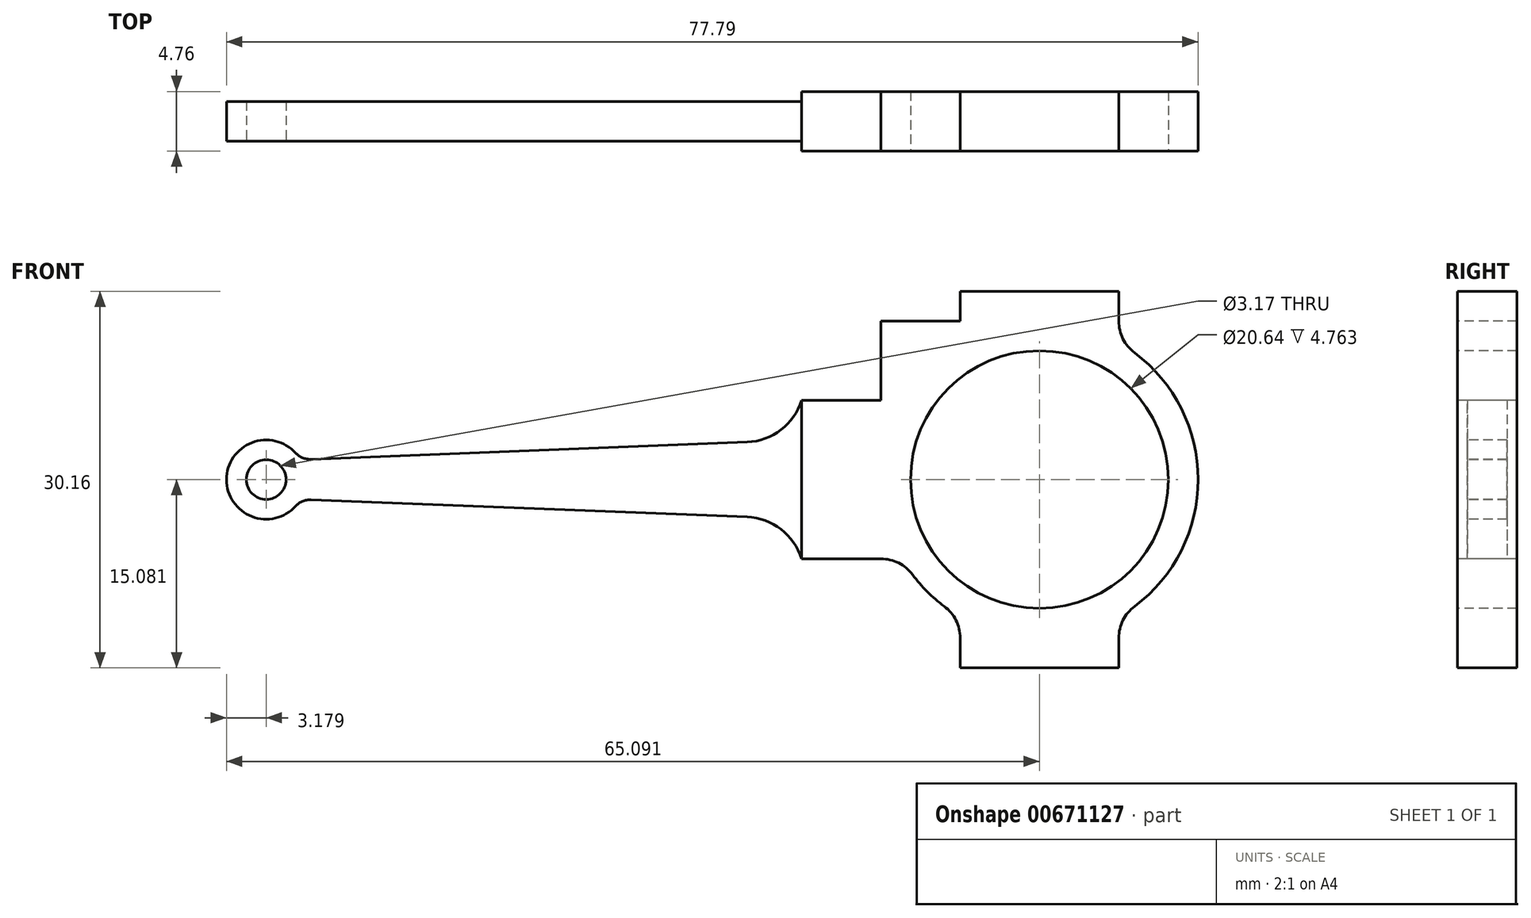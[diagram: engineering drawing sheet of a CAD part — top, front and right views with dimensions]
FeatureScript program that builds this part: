
annotation { "Feature Type Name" : "Feature", "Feature Type Description" : "" }
export const myFeature = defineFeature(function(context is Context, id is Id, definition is map)
    precondition{}
    {
        {
            var Q0;
            Q0=qCreatedBy(makeId("Top.planeOp"),FACE);
            var sketch = newSketch(context, id + "F0", { "sketchPlane" : qUnion([Q0])});
            skLineSegment(sketch, "E0", {"start": v(-28.4, 19.75) * mm, "end": v(17.64, 19.75) * mm});
            skLineSegment(sketch, "E1", {"start": v(17.64, 19.75) * mm, "end": v(17.64, 20.54) * mm});
            skLineSegment(sketch, "E2", {"start": v(17.64, 20.54) * mm, "end": v(49.4, 20.54) * mm});
            skLineSegment(sketch, "E3", {"start": v(49.4, 20.54) * mm, "end": v(49.4, 15.78) * mm});
            skLineSegment(sketch, "E4", {"start": v(49.4, 15.78) * mm, "end": v(17.64, 15.78) * mm});
            skLineSegment(sketch, "E5", {"start": v(17.64, 15.78) * mm, "end": v(17.64, 16.57) * mm});
            skLineSegment(sketch, "E6", {"start": v(17.64, 16.57) * mm, "end": v(-28.4, 16.57) * mm});
            skLineSegment(sketch, "E7", {"start": v(-28.4, 16.57) * mm, "end": v(-28.4, 19.75) * mm});
            skSolve(sketch);
        }
        {
            var Q0;
            Q0=qSketchRegion(id+"F0",true);
            extrude(context, id + "F1", {"entities" : qUnion([Q0]), "depth" : 30.16 * mm});
        }
        {
            var Q0;
            Q0=makeQuery(id+"F1.opExtrude","SWEPT_FACE",FACE,{"disambiguationData":[OSD([sQuery(id+"F0.wireOp",EDGE,"E6")])]});
            var sketch = newSketch(context, id + "F2", { "sketchPlane" : qUnion([Q0])});
            skCircle(sketch, "E8", {"center": v(-25.22, 15.08) * mm, "radius": 1.59 * mm});
            skCircle(sketch, "E9", {"center": v(-25.22, 15.08) * mm, "radius": 3.18 * mm});
            skLineSegment(sketch, "E10", {"start": v(-25.22, 15.08) * mm, "end": v(17.64, 15.08) * mm, "construction": true});
            skLineSegment(sketch, "E11", {"start": v(-22.47, 16.67) * mm, "end": v(17.64, 18.26) * mm});
            skLineSegment(sketch, "E12", {"start": v(-22.47, 13.5) * mm, "end": v(17.64, 11.9) * mm});
            skArc(sketch, "E13", {"start": v(-22.87, 17.22) * mm, "mid": v(-22.31, 16.82) * mm, "end": v(-21.64, 16.7) * mm});
            skArc(sketch, "E14", {"start": v(-21.64, 13.46) * mm, "mid": v(-22.31, 13.34) * mm, "end": v(-22.87, 12.94) * mm});
            skArc(sketch, "E15", {"start": v(13.28, 18.08) * mm, "mid": v(16, 19.06) * mm, "end": v(17.64, 21.43) * mm});
            skArc(sketch, "E16", {"start": v(17.64, 8.73) * mm, "mid": v(16, 11.1) * mm, "end": v(13.28, 12.08) * mm});
            skSolve(sketch);
        }
        {
            var Q0;
            Q0=makeQuery(id+"F2.imprint","IMPRINT",FACE,{"disambiguationData":[TD([[makeQuery(id+"F2.imprint","IMPRINT",EDGE,{"derivedFrom":sQuery(id+"F2.wireOp",EDGE,"E8")}),1.0]])]});
            var Q1;
            {var subQ1=sQuery(id+"F2.wireOp",EDGE,"E13");Q1=makeQuery(id+"F2.imprint","IMPRINT",FACE,{"disambiguationData":[TD([[makeQuery(id+"F2.imprint","IMPRINT",EDGE,{"derivedFrom":subQ1}),1.0]])]});}
            var Q2;
            {var subQ1=sQuery(id+"F2.wireOp",EDGE,"E14");Q2=makeQuery(id+"F2.imprint","IMPRINT",FACE,{"disambiguationData":[TD([[makeQuery(id+"F2.imprint","IMPRINT",EDGE,{"derivedFrom":subQ1}),1.0]])]});}
            extrude(context, id + "F3", {"entities" : qUnion([Q0, Q1, Q2]), "operationType" : NewBodyOperationType.REMOVE, "oppositeDirection" : true, "depth" : 25.4 * mm});
        }
        {
            var Q0;
            Q0=makeQuery(id+"F1.opExtrude","SWEPT_FACE",FACE,{"disambiguationData":[OSD([sQuery(id+"F0.wireOp",EDGE,"E4")])]});
            var sketch = newSketch(context, id + "F4", { "sketchPlane" : qUnion([Q0])});
            skCircle(sketch, "E17", {"center": v(36.7, 15.08) * mm, "radius": 10.32 * mm});
            skCircle(sketch, "E18.0", {"center": v(-25.22, 15.08) * mm, "radius": 1.59 * mm});
            skCircle(sketch, "E19", {"center": v(36.7, 15.08) * mm, "radius": 12.7 * mm});
            skArc(sketch, "E20.0", {"start": v(13.28, 18.08) * mm, "mid": v(16, 19.06) * mm, "end": v(17.64, 21.43) * mm});
            skArc(sketch, "E21.0", {"start": v(17.64, 8.73) * mm, "mid": v(16, 11.1) * mm, "end": v(13.28, 12.08) * mm});
            skLineSegment(sketch, "E22", {"start": v(17.64, 8.73) * mm, "end": v(25.7, 8.73) * mm});
            skLineSegment(sketch, "E23", {"start": v(17.64, 21.43) * mm, "end": v(24, 21.43) * mm});
            skLineSegment(sketch, "E24", {"start": v(24, 21.43) * mm, "end": v(24, 27.78) * mm});
            skLineSegment(sketch, "E25", {"start": v(24, 27.78) * mm, "end": v(30.34, 27.78) * mm});
            skLineSegment(sketch, "E26", {"start": v(30.34, 27.78) * mm, "end": v(30.34, 30.16) * mm});
            skLineSegment(sketch, "E27", {"start": v(30.34, 0) * mm, "end": v(30.34, 4.08) * mm});
            skLineSegment(sketch, "E28", {"start": v(43.04, 30.16) * mm, "end": v(43.04, 26.08) * mm});
            skLineSegment(sketch, "E29", {"start": v(43.04, 0) * mm, "end": v(43.04, 4.08) * mm});
            skArc(sketch, "E30", {"start": v(43.04, 27.78) * mm, "mid": v(43.38, 26.36) * mm, "end": v(44.31, 25.24) * mm});
            skArc(sketch, "E31", {"start": v(26.53, 7.46) * mm, "mid": v(25.41, 8.4) * mm, "end": v(24, 8.73) * mm});
            skArc(sketch, "E32", {"start": v(30.34, 2.38) * mm, "mid": v(30, 3.8) * mm, "end": v(29.07, 4.92) * mm});
            skArc(sketch, "E33", {"start": v(44.31, 4.92) * mm, "mid": v(43.38, 3.8) * mm, "end": v(43.04, 2.38) * mm});
            skSolve(sketch);
        }
        {
            var Q0;
            Q0=makeQuery(id+"F4.imprint","IMPRINT",FACE,{"disambiguationData":[TD([[makeQuery(id+"F4.imprint","IMPRINT",EDGE,{"derivedFrom":sQuery(id+"F4.wireOp",EDGE,"E18.0")}),1.0]])]});
            var Q1;
            {var subQ8=sQuery(id+"F4.wireOp",EDGE,"E30");Q1=makeQuery(id+"F4.imprint","IMPRINT",FACE,{"disambiguationData":[TD([[makeQuery(id+"F4.imprint","IMPRINT",EDGE,{"derivedFrom":subQ8}),1.0]])]});}
            var Q2;
            {var subQ5=sQuery(id+"F4.wireOp",EDGE,"E23");Q2=makeQuery(id+"F4.imprint","IMPRINT",FACE,{"disambiguationData":[TD([[makeQuery(id+"F4.imprint","IMPRINT",EDGE,{"derivedFrom":subQ5}),1.0]])]});}
            var Q3;
            {var subQ8=sQuery(id+"F4.wireOp",EDGE,"E33");Q3=makeQuery(id+"F4.imprint","IMPRINT",FACE,{"disambiguationData":[TD([[makeQuery(id+"F4.imprint","IMPRINT",EDGE,{"derivedFrom":subQ8}),1.0]])]});}
            var Q4;
            {var subQ0=sQuery(id+"F4.wireOp",EDGE,"E31");Q4=makeQuery(id+"F4.imprint","IMPRINT",FACE,{"disambiguationData":[TD([[makeQuery(id+"F4.imprint","IMPRINT",EDGE,{"derivedFrom":subQ0}),1.0]])]});}
            var Q5;
            Q5=makeQuery(id+"F4.imprint","IMPRINT",FACE,{"disambiguationData":[TD([[makeQuery(id+"F4.imprint","IMPRINT",EDGE,{"derivedFrom":sQuery(id+"F4.wireOp",EDGE,"E17")}),1.0]])]});
            extrude(context, id + "F5", {"entities" : qUnion([Q0, Q1, Q2, Q3, Q4, Q5]), "operationType" : NewBodyOperationType.REMOVE, "oppositeDirection" : true, "depth" : 25.4 * mm});
        }
    });
